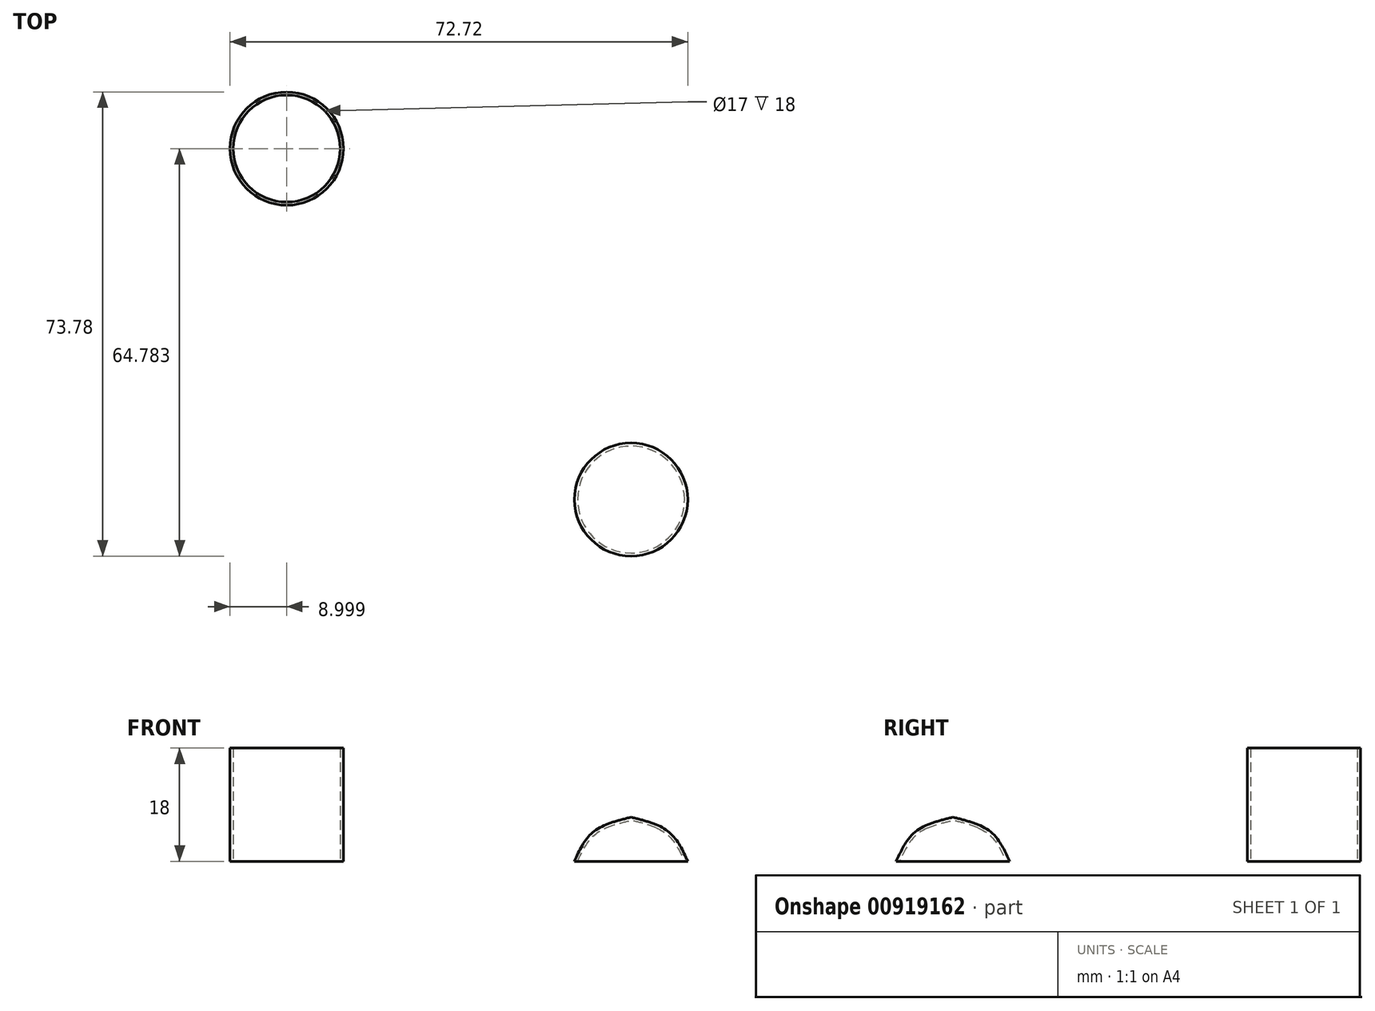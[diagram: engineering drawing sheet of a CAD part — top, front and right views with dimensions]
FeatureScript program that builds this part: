
annotation { "Feature Type Name" : "Feature", "Feature Type Description" : "" }
export const myFeature = defineFeature(function(context is Context, id is Id, definition is map)
    precondition{}
    {
        {
            var Q0;
            Q0=qCreatedBy(makeId("Top.planeOp"),FACE);
            var sketch = newSketch(context, id + "F0", { "sketchPlane" : qUnion([Q0])});
            skCircle(sketch, "E0", {"center": v(-54.72, 55.78) * mm, "radius": 9 * mm});
            skCircle(sketch, "E1.0", {"center": v(-54.72, 55.78) * mm, "radius": 8.5 * mm});
            skSolve(sketch);
        }
        {
            var Q0;
            Q0=makeQuery(id+"F0.imprint","IMPRINT",FACE,{"disambiguationData":[TD([[makeQuery(id+"F0.imprint","IMPRINT",EDGE,{"derivedFrom":sQuery(id+"F0.wireOp",EDGE,"E0")}),1.0]])]});
            extrude(context, id + "F1", {"entities" : qUnion([Q0]), "depth" : 18 * mm, "offsetDistance" : 25.4 * mm});
        }
        {
            var Q0;
            Q0=qCreatedBy(makeId("Front.planeOp"),FACE);
            var sketch = newSketch(context, id + "F2", { "sketchPlane" : qUnion([Q0])});
            skLineSegment(sketch, "E2.bottom", {"start": v(-9, 0) * mm, "end": v(-8.5, 0) * mm});
            skLineSegment(sketch, "E2.right", {"start": v(0, 0) * mm, "end": v(0, 7) * mm});
            skPoint(sketch, "E3", {"position": v(-6, 4.67) * mm});
            skPoint(sketch, "E4", {"position": v(-4, 7) * mm});
            skFitSpline(sketch, "E5", {"points": [v(-9, 0) * mm, v(-6, 4.67) * mm, v(0, 7) * mm], "startDerivative": vector(4.95, 10.94) * mm, "endDerivative": vector(12.95, 3.15) * mm});
            skLineSegment(sketch, "E6", {"start": v(-4, 5.82) * mm, "end": v(-4, 5.3) * mm});
            skPoint(sketch, "E7.start.orphan", {"position": v(-4.5, 3.5) * mm});
            skPoint(sketch, "E2.left.end.orphan", {"position": v(-9, 7) * mm});
            skPoint(sketch, "E2.top.start.orphan", {"position": v(-4.5, 7) * mm});
            skLineSegment(sketch, "E8", {"start": v(-4, 5.82) * mm, "end": v(-4, 5.32) * mm});
            skLineSegment(sketch, "E9", {"start": v(0, 7) * mm, "end": v(0, 6.5) * mm});
            skPoint(sketch, "E10", {"position": v(-5.6, 4.36) * mm});
            skFitSpline(sketch, "E11", {"points": [v(-8.5, 0) * mm, v(-5.6, 4.36) * mm, v(0, 6.5) * mm], "startDerivative": vector(4.82, 10.2) * mm, "endDerivative": vector(12.1, 2.88) * mm});
            skPoint(sketch, "E12.trimOffspring.start.orphan", {"position": v(-4, 0) * mm});
            skSolve(sketch);
        }
        {
            var Q0;
            Q0=makeQuery(id+"F2.imprint","IMPRINT",FACE,{"disambiguationData":[TD([[makeQuery(id+"F2.imprint","IMPRINT",EDGE,{"derivedFrom":sQuery(id+"F2.wireOp",EDGE,"E5")}),-1.0]])]});
            var Q1;
            Q1=sQuery(id+"F2.wireOp",EDGE,"E2.right");
            revolve(context, id + "F3", {"surfaceOperationType" : NewSurfaceOperationType.NEW, "entities" : qUnion([Q0]), "axis" : qUnion([Q1]), "revolveType" : RevolveType.FULL});
        }
    });
